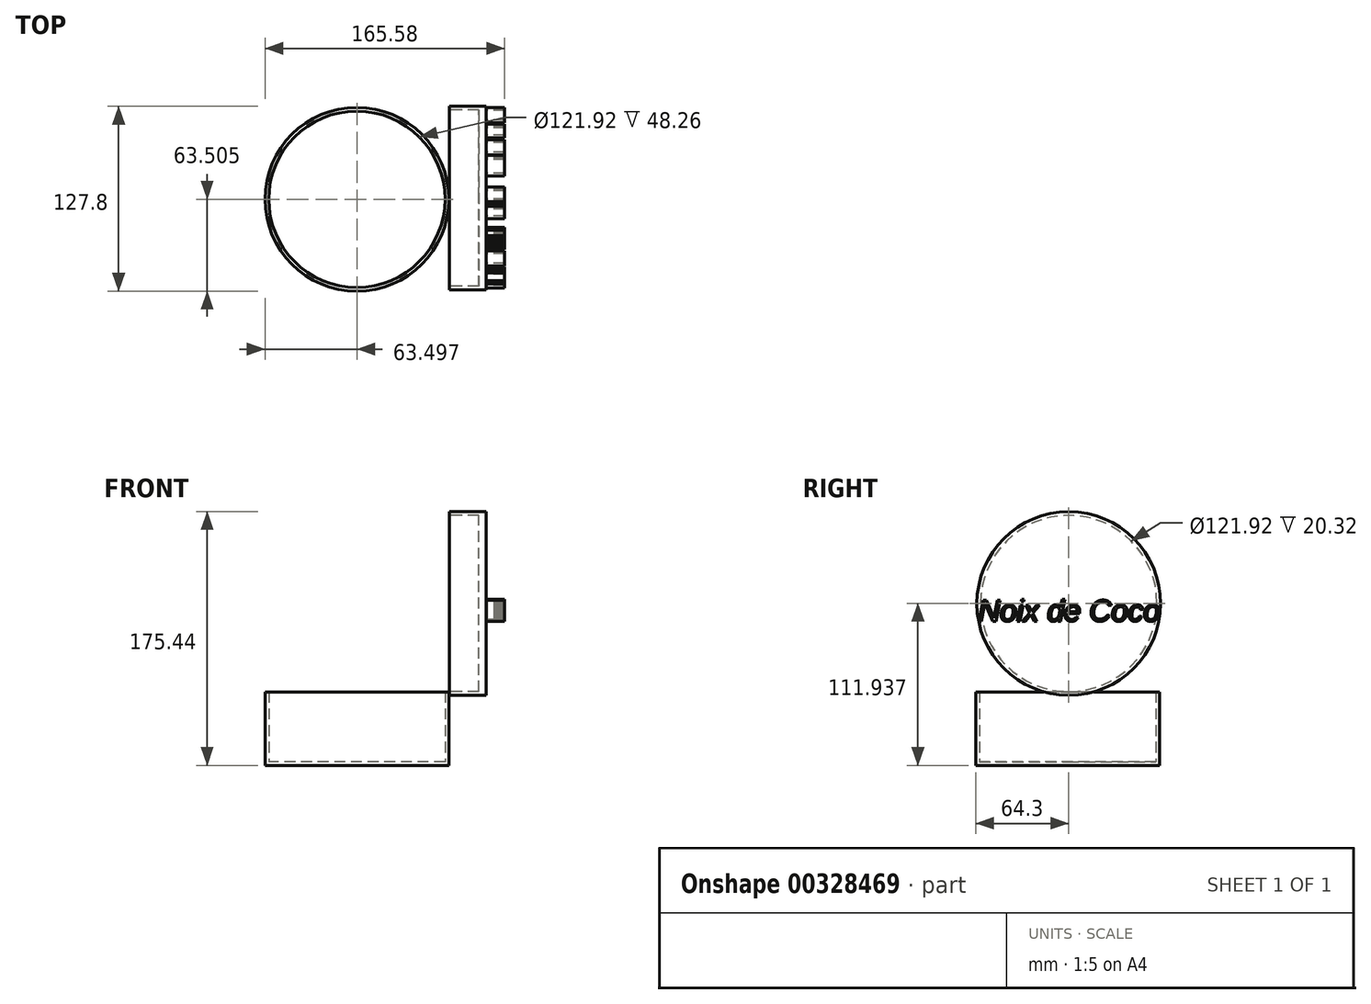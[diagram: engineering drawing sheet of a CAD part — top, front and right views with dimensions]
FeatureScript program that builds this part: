
annotation { "Feature Type Name" : "Feature", "Feature Type Description" : "" }
export const myFeature = defineFeature(function(context is Context, id is Id, definition is map)
    precondition{}
    {
        {
            var Q0;
            Q0=qCreatedBy(makeId("Top.planeOp"),FACE);
            var sketch = newSketch(context, id + "F0", { "sketchPlane" : qUnion([Q0])});
            skCircle(sketch, "E0", {"center": v(-63.98, -98.72) * mm, "radius": 63.5 * mm});
            skSolve(sketch);
        }
        {
            var Q0;
            Q0 = qSketchRegion(id + "F0", true);
            extrude(context, id + "F1", {"entities" : qUnion([Q0]), "depth" : 50.8 * mm});
        }
        {
            var Q0;
            Q0=makeQuery(id+"F1.opExtrude","CAP_FACE",FACE,{"disambiguationData":[OSD([sQuery(id+"F0.wireOp",EDGE,"E0")])],"isStart":false});
            shell(context, id + "F2", {"entities" : qUnion([Q0]), "thickness" : 2.54 * mm});
        }
        {
            var Q0;
            Q0=qCreatedBy(makeId("Right.planeOp"),FACE);
            var sketch = newSketch(context, id + "F3", { "sketchPlane" : qUnion([Q0])});
            skCircle(sketch, "E1", {"center": v(-97.92, 111.94) * mm, "radius": 63.5 * mm});
            skSolve(sketch);
        }
        {
            var Q0;
            Q0 = qSketchRegion(id + "F3", true);
            extrude(context, id + "F4", {"entities" : qUnion([Q0]), "depth" : 25.4 * mm});
        }
        {
            var Q0;
            Q0=makeQuery(id+"F4.opExtrude","CAP_FACE",FACE,{"disambiguationData":[OSD([sQuery(id+"F3.wireOp",EDGE,"E1")])],"isStart":true});
            shell(context, id + "F5", {"entities" : qUnion([Q0]), "thickness" : 2.54 * mm});
        }
        {
            var Q0;
            {var subQ0=sQuery(id+"F3.wireOp",EDGE,"E1");Q0=makeQuery(id+"F5.opShell","OFFSET_FACE",FACE,{"disambiguationData":[OSD([subQ0]),TDD([makeQuery(id+"F4.opExtrude","CAP_FACE",FACE,{"disambiguationData":[OSD([subQ0])],"isStart":false})])]});}
            extrude(context, id + "F6", {"entities" : qUnion([Q0]), "operationType" : NewBodyOperationType.ADD, "depth" : 2.54 * mm});
        }
        {
            var Q0;
            Q0=makeQuery(id+"F4.opExtrude","CAP_FACE",FACE,{"disambiguationData":[OSD([sQuery(id+"F3.wireOp",EDGE,"E1")])],"isStart":false});
            var sketch = newSketch(context, id + "F7", { "sketchPlane" : qUnion([Q0])});
            skText(sketch, "E2", { "text": "Noix de Coco", "fontName": "Arimo-Italic.ttf"});
            const initialGuessF7  = {"E2": [-0.16065, 0.09972, 1, 0, 0.0151]};
            skSetInitialGuess(sketch, initialGuessF7);
            skSolve(sketch);
        }
        {
            var Q0;
            Q0 = qSketchRegion(id + "F7", true);
            extrude(context, id + "F8", {"entities" : qUnion([Q0]), "operationType" : NewBodyOperationType.ADD, "depth" : 12.7 * mm});
        }
    });
